# Revit family: Arper_Nuur-Office_3D_table_160x79cm_0826
name_source: partatom
category: Furniture
units: mm (PartAtom-declared; Revit-internal decimal feet)

## family parameters
Always vertical = Yes
Cut with Voids When Loaded = No
OmniClass Number = 23.40.20.00
OmniClass Title = General Furniture and Specialties
Room Calculation Point = No
Shared = No
Work Plane-Based = No

## types (1)
- Arper_Nuur-Office_3D_table_160x79cm_0826
    Arper - Nuur accessory = Arper - White Metal
    Arper - Top material = Arper - wood white
    Default Elevation = 0 cm
    Description = Office table with a 160 x 79 cm rectangular top fitted with two openings to be used with cable grommet (Art. 0811)  or grommet cover (Art. 0821). Other office accessories complete the composition. The top is made of veneered reconstituted MDF (1,5 cm thick) with a powdercoated aluminium frame. The base and the top are available in a single-colour combination. Height 74 cm.
    Keynote = table
    Manufacturer = ARPER s.p.a.
    Model = Nuur
    Nuur cable holder = Yes
    Nuur freestanding screen = Yes
    Nuur modesty panel = Yes
    Nuur pc holder left = Yes
    Nuur pc holder right = Yes
    URL = http://www.arper.com
